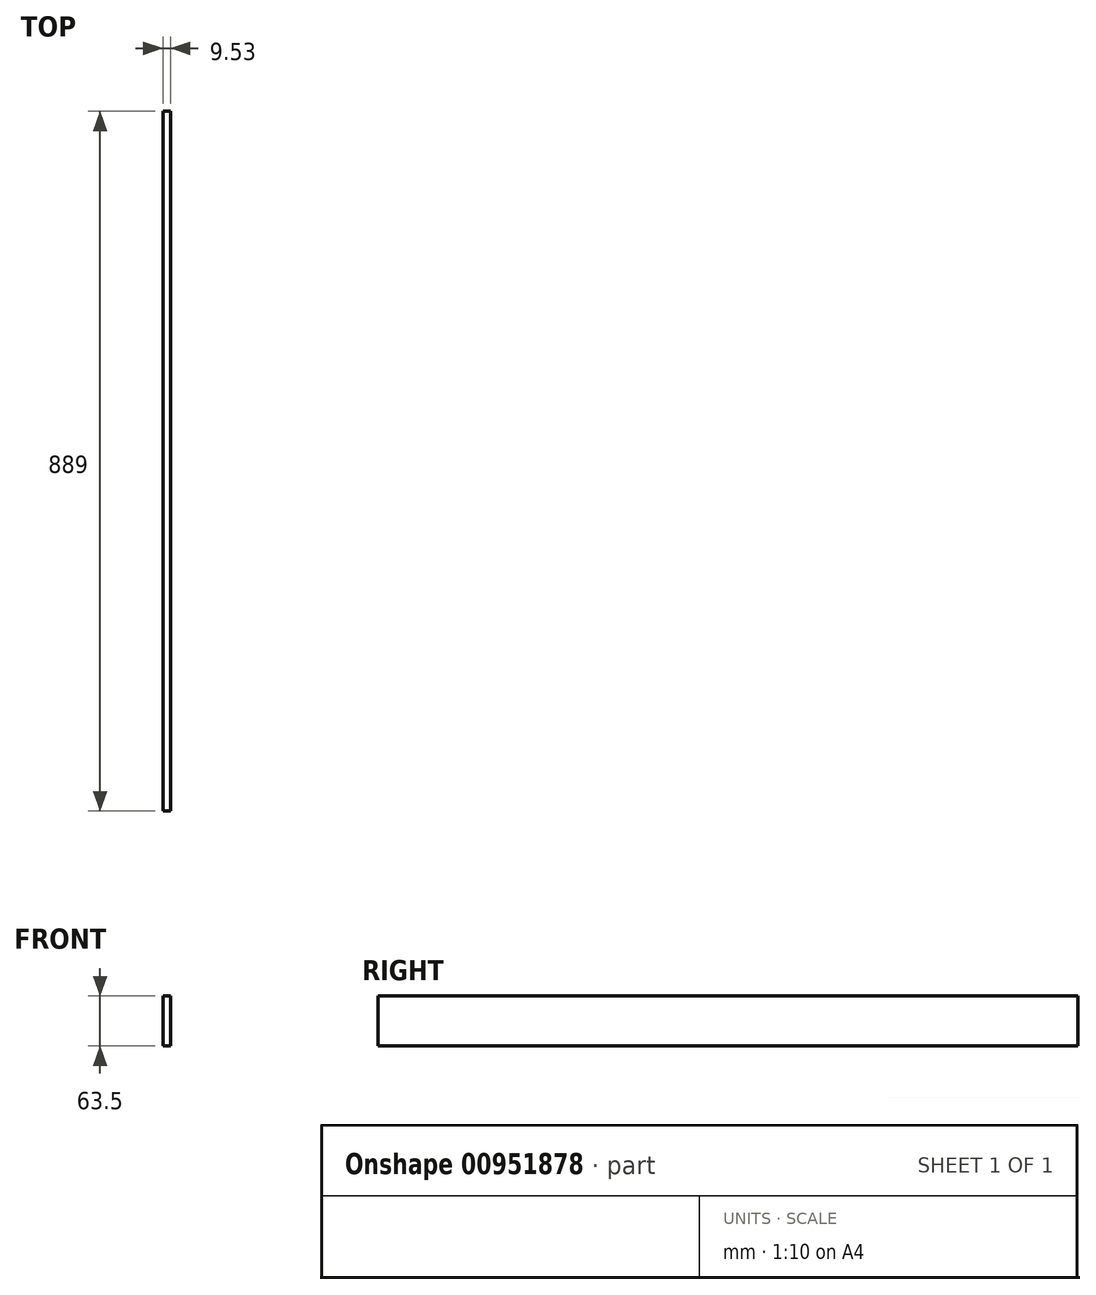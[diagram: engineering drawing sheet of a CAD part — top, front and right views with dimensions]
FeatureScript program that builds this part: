
annotation { "Feature Type Name" : "Feature", "Feature Type Description" : "" }
export const myFeature = defineFeature(function(context is Context, id is Id, definition is map)
    precondition{}
    {
        {
            var Q0;
            Q0=qCreatedBy(makeId("Right.planeOp"),FACE);
            var sketch = newSketch(context, id + "F0", { "sketchPlane" : qUnion([Q0])});
            skLineSegment(sketch, "E0.bottom", {"start": v(444.5, 31.75) * mm, "end": v(-444.5, 31.75) * mm});
            skLineSegment(sketch, "E0.top", {"start": v(444.5, -31.75) * mm, "end": v(-444.5, -31.75) * mm});
            skLineSegment(sketch, "E0.left", {"start": v(444.5, 31.75) * mm, "end": v(444.5, -31.75) * mm});
            skLineSegment(sketch, "E0.right", {"start": v(-444.5, 31.75) * mm, "end": v(-444.5, -31.75) * mm});
            skPoint(sketch, "E0.middle", {"position": v(0, 0) * mm});
            skSolve(sketch);
        }
        {
            var Q0;
            Q0 = qSketchRegion(id + "F0", true);
            extrude(context, id + "F1", {"entities" : qUnion([Q0]), "depth" : 9.52 * mm, "offsetDistance" : 25.4 * mm});
        }
    });
